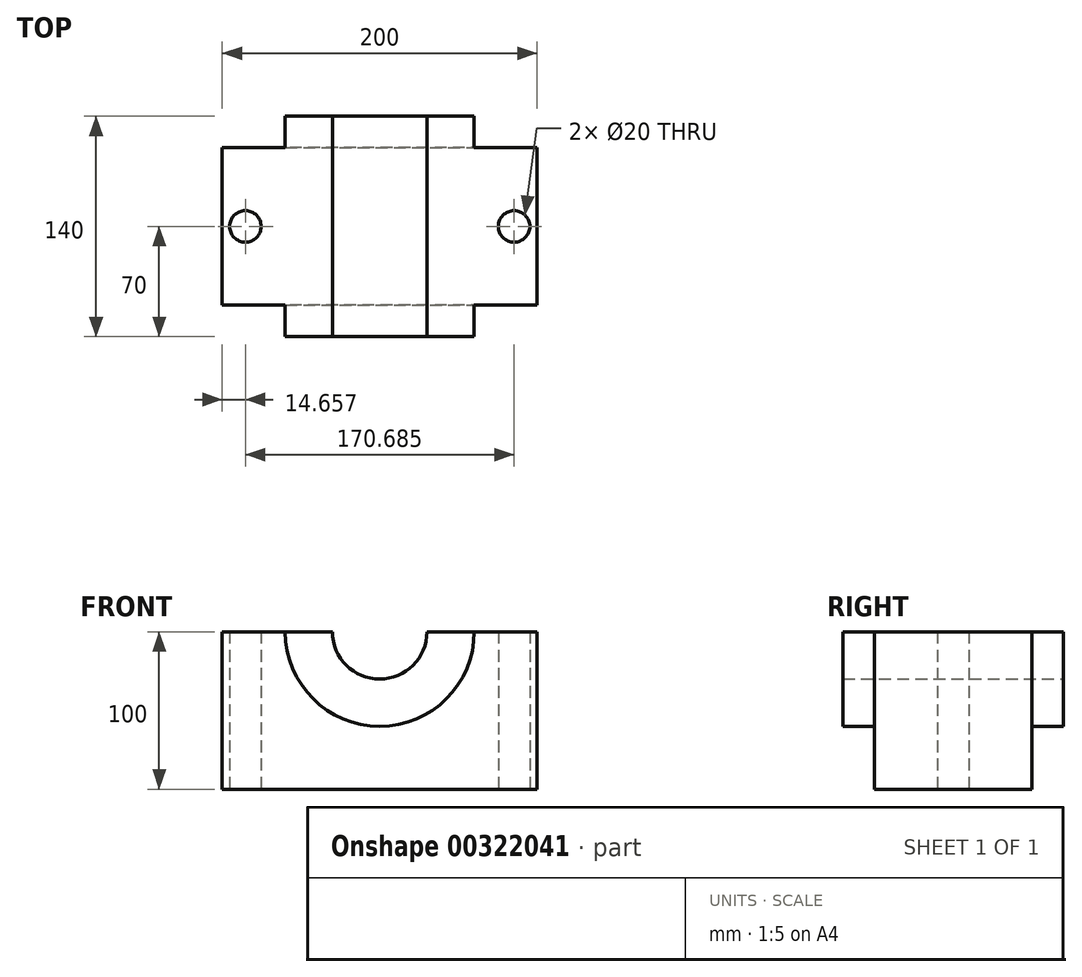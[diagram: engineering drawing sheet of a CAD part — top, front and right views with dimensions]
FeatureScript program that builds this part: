
annotation { "Feature Type Name" : "Feature", "Feature Type Description" : "" }
export const myFeature = defineFeature(function(context is Context, id is Id, definition is map)
    precondition{}
    {
        {
            var Q0;
            Q0=qCreatedBy(makeId("Top.planeOp"),FACE);
            var sketch = newSketch(context, id + "F0", { "sketchPlane" : qUnion([Q0])});
            skLineSegment(sketch, "E0.top", {"start": v(0, -50) * mm, "end": v(-100, -50) * mm});
            skLineSegment(sketch, "E0.right", {"start": v(-100, 0) * mm, "end": v(-100, -50) * mm});
            skPoint(sketch, "E0.middle", {"position": v(0, 0) * mm});
            skLineSegment(sketch, "E1", {"start": v(0, 0) * mm, "end": v(0, -50) * mm});
            skArc(sketch, "E2", {"start": v(-95.34, 0) * mm, "mid": v(-85.34, -10) * mm, "end": v(-75.34, 0) * mm});
            skLineSegment(sketch, "E3", {"start": v(0, 0) * mm, "end": v(-75.34, 0) * mm});
            skPoint(sketch, "E4.orphan", {"position": v(-100, 50) * mm});
            skPoint(sketch, "E5.orphan", {"position": v(0, 50) * mm});
            skPoint(sketch, "E0.left.start.orphan", {"position": v(100, 50) * mm});
            skPoint(sketch, "E6.orphan", {"position": v(100, -50) * mm});
            skLineSegment(sketch, "E7.trimOffspring", {"start": v(-95.34, 0) * mm, "end": v(-100, 0) * mm});
            skSolve(sketch);
        }
        {
            var Q0;
            Q0 = qSketchRegion(id + "F0", true);
            extrude(context, id + "F1", {"entities" : qUnion([Q0]), "depth" : 100 * mm});
        }
        {
            var Q0;
            Q0=makeQuery(id+"F1.opExtrude","SWEPT_FACE",FACE,{"disambiguationData":[OSD([sQuery(id+"F0.wireOp",EDGE,"E0.top")])]});
            var sketch = newSketch(context, id + "F2", { "sketchPlane" : qUnion([Q0])});
            skArc(sketch, "E8", {"start": v(-30, 100) * mm, "mid": v(-21.21, 78.79) * mm, "end": v(0, 70) * mm});
            skArc(sketch, "E9", {"start": v(-60, 100) * mm, "mid": v(-42.43, 57.57) * mm, "end": v(0, 40) * mm});
            skSolve(sketch);
        }
        {
            var Q0;
            {var subQ0=sQuery(id+"F2.wireOp",EDGE,"E8");Q0=makeQuery(id+"F2.imprint","IMPRINT",FACE,{"disambiguationData":[TD([[makeQuery(id+"F2.imprint","IMPRINT",EDGE,{"derivedFrom":subQ0}),-1.0]])]});}
            extrude(context, id + "F3", {"entities" : qUnion([Q0]), "operationType" : NewBodyOperationType.ADD, "depth" : 20 * mm});
        }
        {
            var Q0;
            {var subQ1=sQuery(id+"F0.wireOp",EDGE,"E0.top");Q0=makeQuery(id+"F3.boolean.opBoolean","SPLIT",FACE,{"disambiguationData":[TD([makeQuery(id+"F3.opExtrude","SWEPT_FACE",FACE,{"disambiguationData":[OSD([sQuery(id+"F2.wireOp",EDGE,"E8")])]})])],"derivedFrom":makeQuery(id+"F1.opExtrude","SWEPT_FACE",FACE,{"disambiguationData":[OSD([subQ1])]})});}
            var Q1;
            Q1=makeQuery(id+"F1.opExtrude","SWEPT_FACE",FACE,{"disambiguationData":[OSD([sQuery(id+"F0.wireOp",EDGE,"E3")])]});
            extrude(context, id + "F4", {"entities" : qUnion([Q0]), "operationType" : NewBodyOperationType.REMOVE, "endBound" : BoundingType.UP_TO_SURFACE, "oppositeDirection" : true, "endBoundEntityFace" : qUnion([Q1]), "depth" : 25 * mm});
        }
        {
            var Q0;
            Q0=makeQuery(id+"F1.opExtrude","SWEPT_BODY",BODY,{"disambiguationData":[OSD([sQuery(id+"F0.wireOp",EDGE,"E0.top"),sQuery(id+"F0.wireOp",EDGE,"E0.right"),sQuery(id+"F0.wireOp",EDGE,"E1"),sQuery(id+"F0.wireOp",EDGE,"E2"),sQuery(id+"F0.wireOp",EDGE,"E3"),sQuery(id+"F0.wireOp",EDGE,"E7.trimOffspring")])]});
            var Q1;
            Q1=qCreatedBy(makeId("Front.planeOp"),FACE);
            mirror(context, id + "F5", {"operationType" : NewBodyOperationType.ADD, "entities" : qUnion([Q0]), "mirrorPlane" : qUnion([Q1])});
        }
        {
            var Q0;
            Q0=makeQuery(id+"F1.opExtrude","SWEPT_BODY",BODY,{"disambiguationData":[OSD([sQuery(id+"F0.wireOp",EDGE,"E0.top"),sQuery(id+"F0.wireOp",EDGE,"E0.right"),sQuery(id+"F0.wireOp",EDGE,"E1"),sQuery(id+"F0.wireOp",EDGE,"E2"),sQuery(id+"F0.wireOp",EDGE,"E3"),sQuery(id+"F0.wireOp",EDGE,"E7.trimOffspring")])]});
            var Q1;
            {var subQ0=sQuery(id+"F0.wireOp",EDGE,"E1");var subQ1=makeQuery(id+"F3.boolean.opBoolean","MERGE",FACE,{"derivedFrom":[makeQuery(id+"F1.opExtrude","SWEPT_FACE",FACE,{"disambiguationData":[OSD([subQ0])]}),makeQuery(id+"F3.opExtrude","SWEPT_FACE",FACE,{"disambiguationData":[OSD([sQuery(id+"F0.wireOp",EDGE,"E0.top"),subQ0])]})]});Q1=makeQuery(id+"F5.boolean.opBoolean","MERGE",FACE,{"derivedFrom":[subQ1,makeQuery(id+"F5.opPattern","COPY",FACE,{"derivedFrom":subQ1,"instanceName":"1"})]});}
            mirror(context, id + "F6", {"operationType" : NewBodyOperationType.ADD, "entities" : qUnion([Q0]), "mirrorPlane" : qUnion([Q1])});
        }
    });
